# Revit family: Window_Shade-Draper-LightBloc_Zip
name_source: partatom
category: Specialty Equipment
units: mm (PartAtom-declared; Revit-internal decimal feet)

## family parameters
Always vertical = Yes
Classification Number = 23.30.60.14.21
Cut with Voids When Loaded = No
Enable Cutting in Views = No
Maintain Annotation Orientation = No
Part Type = Normal
Room Calculation Point = No
Round Connector Dimension = Use Diameter
Shared = No
Work Plane-Based = No

## types (6) — shared parameters
Casing = Metal - Draper - Silver
Default Elevation = 0"
Description = Wind Resistant Roller Shade
Manufacturer = Draper
Model = LightBloc
Multiple Units = A Maximum of 3 Panels can be added together.
Product Documentation Link = http://www.draperinc.com
Product Name = LightBloc Zip
Product Page URL = http://www.draperinc.com
Shade Fabric = Fiberglass - Draper - Fabric - Screen
URL = http://www.draperinc.com
Wind Note = Very wind resistant.  Wind tunnel tested up to 90 MPH.

## per-type parameters (varying)
| type | 105 Style Headbox | 125 Style Headbox | Curved Headbox Design | Square Headbox Design | Standard Headbox Design |
| 105 Curve Headbox Design | Yes | No | Yes | No | No |
| 125 Curve Headbox Design | No | Yes | Yes | No | No |
| 105 Standard Headbox Design | Yes | No | No | No | Yes |
| 125 Standard Headbox Design | No | Yes | No | No | Yes |
| 105 Square Headbox Design | Yes | No | No | Yes | No |
| 125 Square Headbox Design | No | Yes | No | Yes | No |

## geometry (parser evidence)
native form markers: Sweep x2
no freeform markers — native parametric forms only
